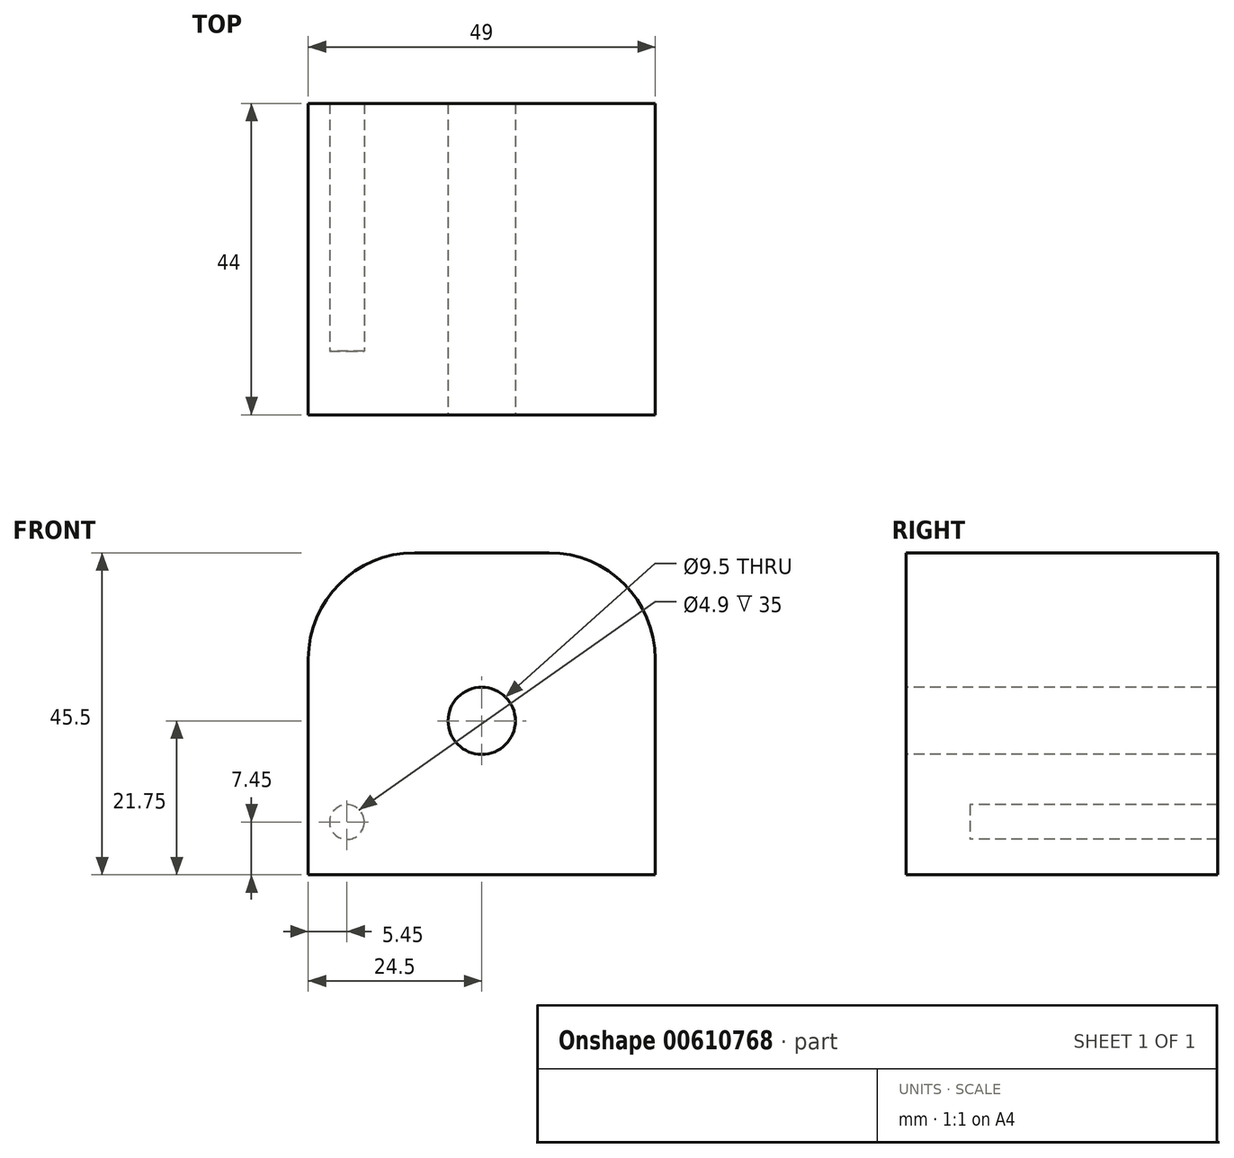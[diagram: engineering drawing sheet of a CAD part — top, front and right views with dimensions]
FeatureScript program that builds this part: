
annotation { "Feature Type Name" : "Feature", "Feature Type Description" : "" }
export const myFeature = defineFeature(function(context is Context, id is Id, definition is map)
    precondition{}
    {
        {
            var Q0;
            Q0=qCreatedBy(makeId("Front.planeOp"),FACE);
            var sketch = newSketch(context, id + "F0", { "sketchPlane" : qUnion([Q0])});
            skLineSegment(sketch, "E0.bottom", {"start": v(24.5, -22.75) * mm, "end": v(-24.5, -22.75) * mm});
            skLineSegment(sketch, "E0.top", {"start": v(9.5, 22.75) * mm, "end": v(-9.5, 22.75) * mm});
            skLineSegment(sketch, "E0.left", {"start": v(24.5, -22.75) * mm, "end": v(24.5, 7.75) * mm});
            skLineSegment(sketch, "E0.right", {"start": v(-24.5, -22.75) * mm, "end": v(-24.5, 7.75) * mm});
            skPoint(sketch, "E0.middle", {"position": v(0, 0) * mm});
            skPoint(sketch, "E1.visualSharp", {"position": v(24.5, 22.75) * mm});
            skArc(sketch, "E1.filletArc", {"start": v(24.5, 7.75) * mm, "mid": v(20.1, 18.36) * mm, "end": v(9.5, 22.75) * mm});
            skPoint(sketch, "E2.visualSharp", {"position": v(-24.5, 22.75) * mm});
            skArc(sketch, "E2.filletArc", {"start": v(-9.5, 22.75) * mm, "mid": v(-20.1, 18.36) * mm, "end": v(-24.5, 7.75) * mm});
            skSolve(sketch);
        }
        {
            var Q0;
            Q0=makeQuery(id+"F0.imprint","IMPRINT",FACE,{"disambiguationData":[TD([[makeQuery(id+"F0.imprint","IMPRINT",EDGE,{"derivedFrom":sQuery(id+"F0.wireOp",EDGE,"E0.bottom")}),-1.0]])]});
            extrude(context, id + "F1", {"entities" : qUnion([Q0]), "depth" : 9 * mm, "offsetDistance" : 25 * mm});
        }
        {
            var Q0;
            Q0=makeQuery(id+"F1.opExtrude","CAP_FACE",FACE,{"disambiguationData":[OSD([sQuery(id+"F0.wireOp",EDGE,"E0.bottom"),sQuery(id+"F0.wireOp",EDGE,"E0.top"),sQuery(id+"F0.wireOp",EDGE,"E0.left"),sQuery(id+"F0.wireOp",EDGE,"E0.right"),sQuery(id+"F0.wireOp",EDGE,"E1.filletArc"),sQuery(id+"F0.wireOp",EDGE,"E2.filletArc")])],"isStart":false});
            var sketch = newSketch(context, id + "F2", { "sketchPlane" : qUnion([Q0])});
            skPoint(sketch, "E3.endSnap0", {"position": v(0, -22.75) * mm});
            skCircle(sketch, "E4", {"center": v(0, -1) * mm, "radius": 4.75 * mm});
            skPoint(sketch, "E3.end.orphan", {"position": v(0, -5.75) * mm});
            skPoint(sketch, "E3.start.orphan", {"position": v(0, -22.75) * mm});
            skSolve(sketch);
        }
        {
            var Q0;
            Q0=makeQuery(id+"F2.imprint","IMPRINT",FACE,{"disambiguationData":[TD([[makeQuery(id+"F2.imprint","IMPRINT",EDGE,{"derivedFrom":sQuery(id+"F2.wireOp",EDGE,"E4")}),1.0]])]});
            extrude(context, id + "F3", {"entities" : qUnion([Q0]), "operationType" : NewBodyOperationType.REMOVE, "oppositeDirection" : true, "depth" : 25 * mm, "offsetDistance" : 25 * mm});
        }
        {
            var Q0;
            Q0=makeQuery(id+"F1.opExtrude","CAP_FACE",FACE,{"disambiguationData":[OSD([sQuery(id+"F0.wireOp",EDGE,"E0.bottom"),sQuery(id+"F0.wireOp",EDGE,"E0.top"),sQuery(id+"F0.wireOp",EDGE,"E0.left"),sQuery(id+"F0.wireOp",EDGE,"E0.right"),sQuery(id+"F0.wireOp",EDGE,"E1.filletArc"),sQuery(id+"F0.wireOp",EDGE,"E2.filletArc")])],"isStart":true});
            var sketch = newSketch(context, id + "F4", { "sketchPlane" : qUnion([Q0])});
            skCircle(sketch, "E5", {"center": v(-19.05, -15.3) * mm, "radius": 2.45 * mm});
            skCircle(sketch, "E6.MirrorC", {"center": v(19.05, -15.3) * mm, "radius": 2.45 * mm});
            skSolve(sketch);
        }
        {
            var Q0;
            Q0=makeQuery(id+"F4.imprint","IMPRINT",FACE,{"disambiguationData":[TD([[makeQuery(id+"F4.imprint","IMPRINT",EDGE,{"derivedFrom":sQuery(id+"F4.wireOp",EDGE,"E5")}),1.0]])]});
            var Q1;
            Q1=makeQuery(id+"F4.imprint","IMPRINT",FACE,{"disambiguationData":[TD([[makeQuery(id+"F4.imprint","IMPRINT",EDGE,{"derivedFrom":sQuery(id+"F4.wireOp",EDGE,"E6.MirrorC")}),-1.0]])]});
            extrude(context, id + "F5", {"entities" : qUnion([Q0, Q1]), "operationType" : NewBodyOperationType.ADD, "depth" : 35 * mm, "offsetDistance" : 25 * mm});
        }
    });
